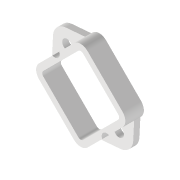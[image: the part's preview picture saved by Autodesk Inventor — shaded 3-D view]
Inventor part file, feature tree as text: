
AUTODESK INVENTOR PART (.ipt)
format: ipt  version: 2022 (Build 260153000, 153)  size: 202,240 bytes
history: native  units: mm
features: reference x4, other x3, extrude x2, sketch x2, projected_geometry x1
ambient origin geometry x8: Origin, YZ Plane, XZ Plane, XY Plane, X Axis, Y Axis, Z Axis, Center Point
bodies: Body1 (feature_tree)
feature tree (12):
  extrude  "Extrusion4"  Depth=3.2mm
  extrude  "Extrusion5"  Depth=4.0mm
  sketch  "Skizze1"  dims[d15=0.1mm d16=3.2mm]
  reference  "Referenz1"
  reference  "Referenz2"
  reference  "Referenz3"
  reference  "Referenz7"
  sketch  "Skizze5"  dims[d17=3.2mm d18=3.0mm d19=3.0mm d20=2.0mm d21=2.0mm d22=0.0mm d23=4.0mm d24=0.0mm]
  projected_geometry  "Projizierte Kontur2"
  other  "Assembly_Matchboxscope_injectionmolded.iam"
  other  "IM_Matchboxscope_base:1"
  other  "00_CCTV_M12_VCM_large:1"
